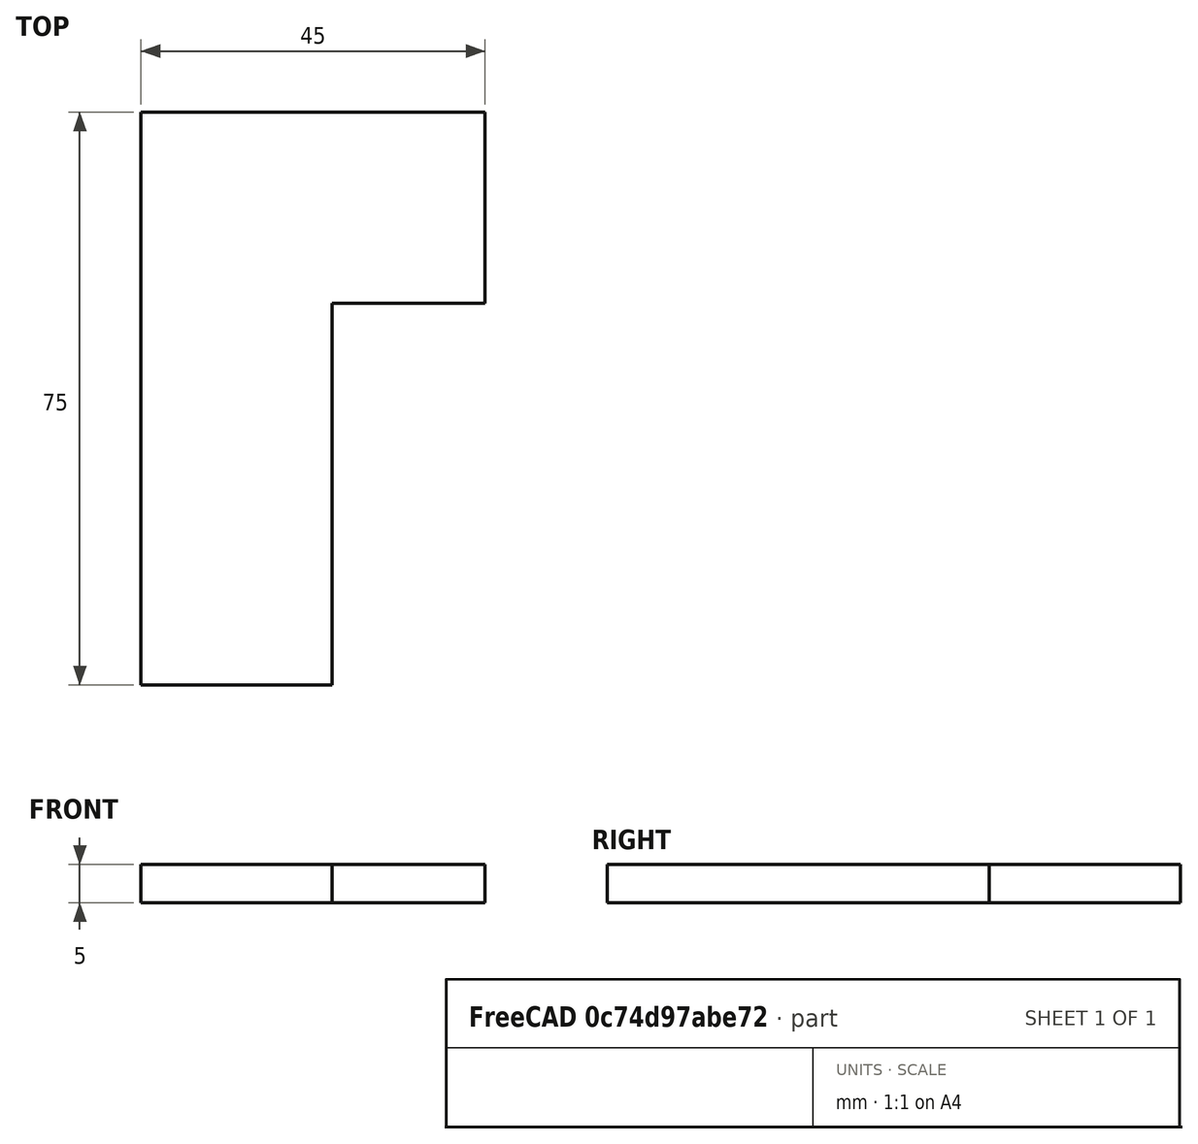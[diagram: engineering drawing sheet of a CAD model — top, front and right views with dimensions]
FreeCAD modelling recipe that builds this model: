
FCSTD DOCUMENT  (FreeCAD 0.21R33694 (Git))
Label: z_end_switch_stop
License: All rights reserved
LicenseURL: http://en.wikipedia.org/wiki/All_rights_reserved
objects: Sketcher::SketchObject×1, PartDesign::Pad×1, PartDesign::Body×1
note: 4 computed .brp shape members not serialized (recipe doc carries the construction recipe); baked Part::Feature solids carry a one-line shape summary decoded from their .brp

FEATURE [Sketcher::SketchObject] Sketch
  FullyConstrained = true
  MapMode = 5
  Support = -> [XY_Plane]
  sketch-geometry (6):
    g0: LineSegment StartX=0 StartY=0 StartZ=0 EndX=25 EndY=0 EndZ=0
    g1: LineSegment StartX=25 StartY=0 StartZ=0 EndX=25 EndY=50 EndZ=0
    g2: LineSegment StartX=25 StartY=50 StartZ=0 EndX=45 EndY=50 EndZ=0
    g3: LineSegment StartX=45 StartY=50 StartZ=0 EndX=45 EndY=75 EndZ=0
    g4: LineSegment StartX=45 StartY=75 StartZ=0 EndX=0 EndY=75 EndZ=0
    g5: LineSegment StartX=0 StartY=75 StartZ=0 EndX=0 EndY=0 EndZ=0
  constraints (17):
    c: Coincident(g0,g-1)
    c: PointOnObject(g0,g-1)
    c: Coincident(g1,g0)
    c: Vertical(g1)
    c: Coincident(g2,g1)
    c: Coincident(g3,g2)
    c: Vertical(g3)
    c: Coincident(g4,g3)
    c: PointOnObject(g4,g-2)
    c: Horizontal(g4)
    c: Coincident(g5,g4)
    c: Coincident(g5,g0)
    c: Horizontal(g2)
    c: DistanceX(g0,g0) = 25
    c: DistanceY(g1,g1) = 50
    c: DistanceY(g3,g3) = 25
    c: DistanceX(g4,g4) = 45
FEATURE [PartDesign::Pad] Pad
  Direction = (0,0,1)
  Length = 5
  Length2 = 10
  Profile = -> Sketch
  ReferenceAxis = -> Sketch [N_Axis]
  Type = 0
FEATURE [PartDesign::Body] Body
  Group = -> [Sketch,Pad]
  Origin = -> Origin
  Tip = -> Pad
